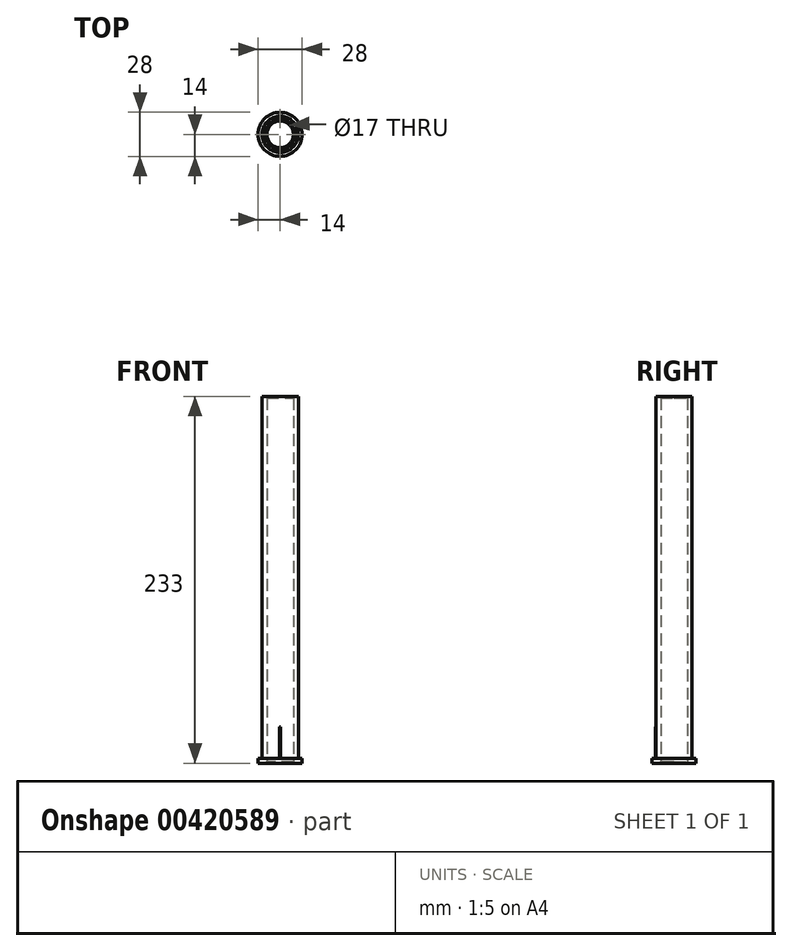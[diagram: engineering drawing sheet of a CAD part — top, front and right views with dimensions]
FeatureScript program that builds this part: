
annotation { "Feature Type Name" : "Feature", "Feature Type Description" : "" }
export const myFeature = defineFeature(function(context is Context, id is Id, definition is map)
    precondition{}
    {
        {
            var Q0;
            Q0=qCreatedBy(makeId("Front.planeOp"),FACE);
            var sketch = newSketch(context, id + "F0", { "sketchPlane" : qUnion([Q0])});
            skLineSegment(sketch, "E0", {"start": v(0, 0) * mm, "end": v(0, 96.12) * mm, "construction": true});
            skLineSegment(sketch, "E1", {"start": v(-8.5, 0) * mm, "end": v(-8.5, 233) * mm});
            skLineSegment(sketch, "E2", {"start": v(-8.5, 233) * mm, "end": v(-11.5, 233) * mm});
            skLineSegment(sketch, "E3", {"start": v(-11.5, 233) * mm, "end": v(-11.5, 3) * mm});
            skLineSegment(sketch, "E4", {"start": v(-11.5, 3) * mm, "end": v(-14, 3) * mm});
            skLineSegment(sketch, "E5", {"start": v(-14, 3) * mm, "end": v(-14, 0) * mm});
            skLineSegment(sketch, "E6", {"start": v(-14, 0) * mm, "end": v(-8.5, 0) * mm});
            skSolve(sketch);
        }
        {
            var Q0;
            Q0 = qSketchRegion(id + "F0", true);
            var Q1;
            Q1=sQuery(id+"F0.wireOp",EDGE,"E0");
            revolve(context, id + "F1", {"entities" : qUnion([Q0]), "axis" : qUnion([Q1]), "revolveType" : RevolveType.FULL});
        }
        {
            var Q0;
            Q0=makeQuery(id+"F1.opRevolve","SWEPT_FACE",FACE,{"disambiguationData":[OSD([sQuery(id+"F0.wireOp",EDGE,"E4")])]});
            var sketch = newSketch(context, id + "F2", { "sketchPlane" : qUnion([Q0])});
            skCircle(sketch, "E7", {"center": v(0, -11.5) * mm, "radius": 0.25 * mm});
            skSolve(sketch);
        }
        {
            var Q0;
            Q0 = qSketchRegion(id + "F2", true);
            extrude(context, id + "F3", {"entities" : qUnion([Q0]), "operationType" : NewBodyOperationType.ADD, "depth" : 20 * mm, "offsetDistance" : 25 * mm});
        }
        {
            var Q0;
            Q0=makeQuery(id+"F1.opRevolve","SWEPT_EDGE",EDGE,{"disambiguationData":[OSD([sQuery(id+"F0.wireOp",EDGE,"E1"),sQuery(id+"F0.wireOp",EDGE,"E6")])]});
            var Q1;
            Q1=makeQuery(id+"F1.opRevolve","SWEPT_EDGE",EDGE,{"disambiguationData":[OSD([sQuery(id+"F0.wireOp",EDGE,"E1"),sQuery(id+"F0.wireOp",EDGE,"E2")])]});
            chamfer(context, id + "F4", {"entities" : qUnion([Q0, Q1]), "width" : 1 * mm, "tangentPropagation" : true});
        }
    });
